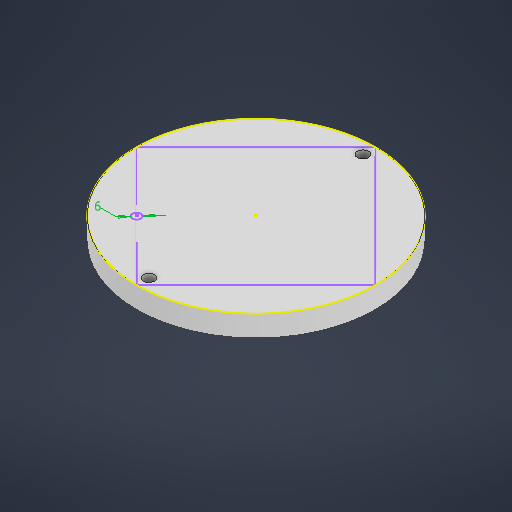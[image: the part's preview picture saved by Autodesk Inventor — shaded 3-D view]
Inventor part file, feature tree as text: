
AUTODESK INVENTOR PART (.ipt)
format: ipt  version: 2025 (Build 290162000, 162)  size: 196,096 bytes
history: native  units: in
note: dims shown in document units (in); Inventor stores cm internally (conversion verified against a paired STEP export)
features: extrude x3, sketch x3, other x1
ambient origin geometry x8: Origin, YZ Plane, XZ Plane, XY Plane, X Axis, Y Axis, Z Axis, Center Point
bodies: Solid1 (feature_tree)
feature tree (7):
  extrude  "Extrusion1"  Depth=0.5906in TaperAngle=0.0deg
  sketch  "Sketch2"  dims[d3=5.9843in d4=0.315in]
  extrude  "Extrusion2"  Depth=0.315in
  extrude  "Extrusion3"  Depth=0.4724in
  other  "Work Axis1"
  sketch  "Sketch3"  dims[d5=0.315in d6=0.1772in d7=0.1772in d8=0.0in d9=0.0in d10=0.4724in d11=0.0in d13=0.2362in]
  sketch  "Sketch1"  dims[d0=6.6732in d1=0.5906in d2=0.0in]
